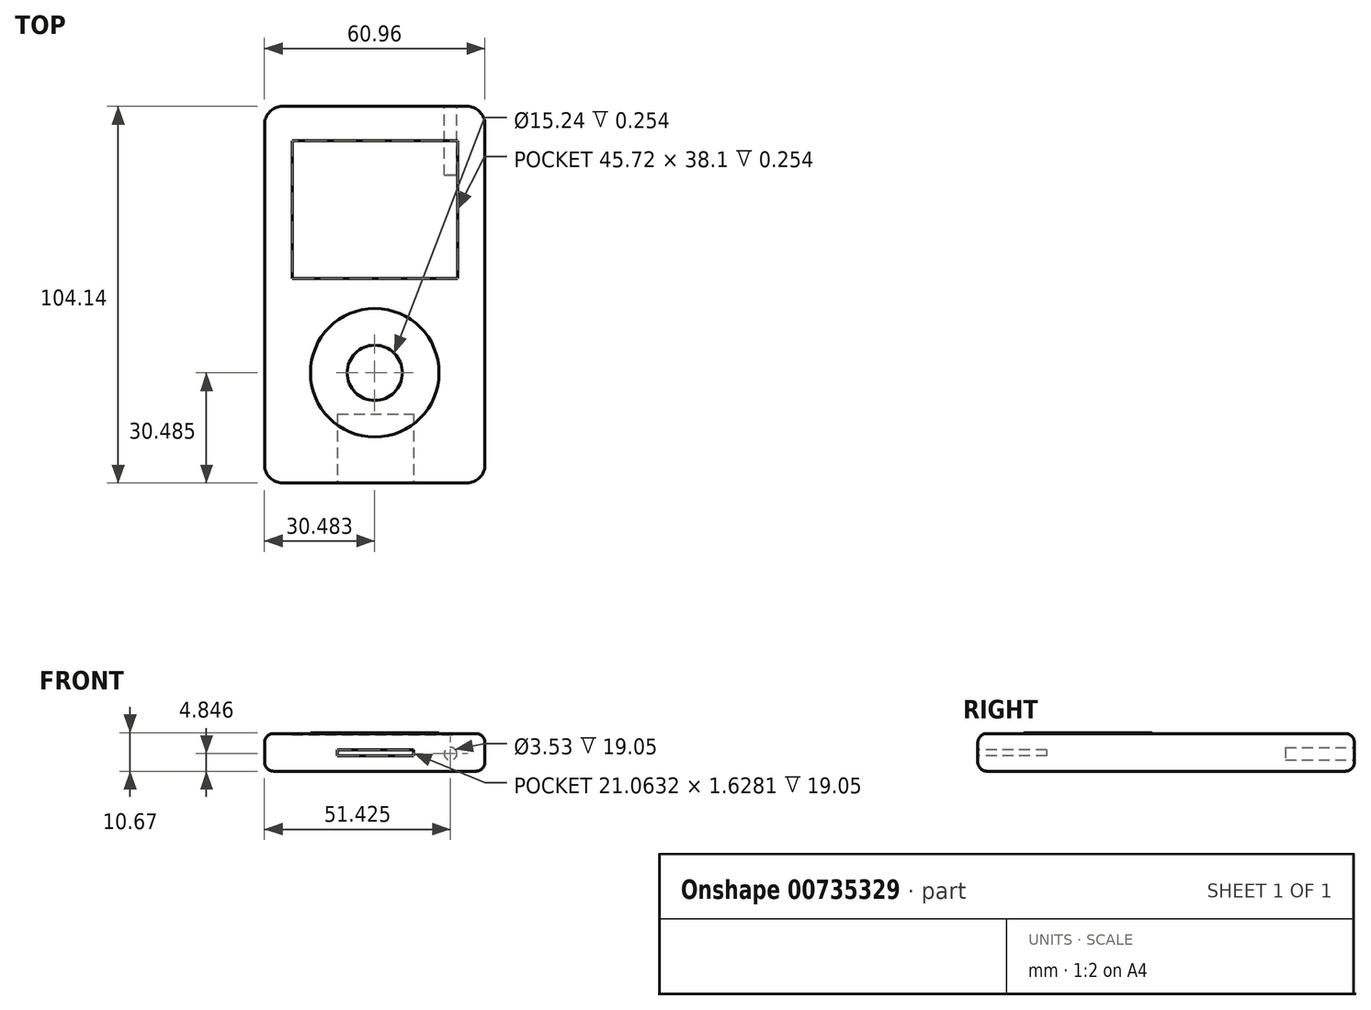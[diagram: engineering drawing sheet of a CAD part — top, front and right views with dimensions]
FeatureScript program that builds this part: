
annotation { "Feature Type Name" : "Feature", "Feature Type Description" : "" }
export const myFeature = defineFeature(function(context is Context, id is Id, definition is map)
    precondition{}
    {
        {
            var Q0;
            Q0=qCreatedBy(makeId("Top.planeOp"),FACE);
            var sketch = newSketch(context, id + "F0", { "sketchPlane" : qUnion([Q0])});
            skLineSegment(sketch, "E0.bottom", {"start": v(-38.1, 48.27) * mm, "end": v(22.85, 48.27) * mm});
            skLineSegment(sketch, "E0.top", {"start": v(-38.1, -55.87) * mm, "end": v(22.85, -55.87) * mm});
            skLineSegment(sketch, "E0.left", {"start": v(-38.1, 48.27) * mm, "end": v(-38.1, -55.87) * mm});
            skLineSegment(sketch, "E0.right", {"start": v(22.85, 48.27) * mm, "end": v(22.85, -55.87) * mm});
            skSolve(sketch);
        }
        {
            var Q0;
            Q0=makeQuery(id+"F0.imprint","IMPRINT",FACE,{"disambiguationData":[TD([[makeQuery(id+"F0.imprint","IMPRINT",EDGE,{"derivedFrom":sQuery(id+"F0.wireOp",EDGE,"E0.bottom")}),-1.0]])]});
            extrude(context, id + "F1", {"entities" : qUnion([Q0]), "depth" : 10.4 * mm, "offsetDistance" : 25.4 * mm});
        }
        {
            var Q0;
            Q0=makeQuery(id+"F1.opExtrude","SWEPT_EDGE",EDGE,{"disambiguationData":[OSD([sQuery(id+"F0.wireOp",EDGE,"E0.bottom"),sQuery(id+"F0.wireOp",EDGE,"E0.right")])]});
            var Q1;
            Q1=makeQuery(id+"F1.opExtrude","SWEPT_EDGE",EDGE,{"disambiguationData":[OSD([sQuery(id+"F0.wireOp",EDGE,"E0.bottom"),sQuery(id+"F0.wireOp",EDGE,"E0.left")])]});
            var Q2;
            Q2=makeQuery(id+"F1.opExtrude","SWEPT_EDGE",EDGE,{"disambiguationData":[OSD([sQuery(id+"F0.wireOp",EDGE,"E0.top"),sQuery(id+"F0.wireOp",EDGE,"E0.right")])]});
            var Q3;
            Q3=makeQuery(id+"F1.opExtrude","SWEPT_EDGE",EDGE,{"disambiguationData":[OSD([sQuery(id+"F0.wireOp",EDGE,"E0.top"),sQuery(id+"F0.wireOp",EDGE,"E0.left")])]});
            fillet(context, id + "F2", {"entities" : qUnion([Q0, Q1, Q2, Q3]), "radius" : 5.08 * mm, "tangentPropagation" : true, "allowEdgeOverflow" : false});
        }
        {
            var Q0;
            Q0=makeQuery(id+"F1.opExtrude","CAP_FACE",FACE,{"disambiguationData":[OSD([sQuery(id+"F0.wireOp",EDGE,"E0.bottom"),sQuery(id+"F0.wireOp",EDGE,"E0.top"),sQuery(id+"F0.wireOp",EDGE,"E0.left"),sQuery(id+"F0.wireOp",EDGE,"E0.right")])],"isStart":false});
            var sketch = newSketch(context, id + "F3", { "sketchPlane" : qUnion([Q0])});
            skCircle(sketch, "E1", {"center": v(-7.63, -25.39) * mm, "radius": 17.78 * mm});
            skCircle(sketch, "E2", {"center": v(-7.63, -25.39) * mm, "radius": 7.62 * mm});
            skSolve(sketch);
        }
        {
            var Q0;
            Q0=makeQuery(id+"F3.imprint","IMPRINT",FACE,{"disambiguationData":[TD([[makeQuery(id+"F3.imprint","IMPRINT",EDGE,{"derivedFrom":sQuery(id+"F3.wireOp",EDGE,"E1")}),1.0]])]});
            extrude(context, id + "F4", {"entities" : qUnion([Q0]), "operationType" : NewBodyOperationType.ADD, "depth" : 0.25 * mm, "offsetDistance" : 25.4 * mm});
        }
        {
            var Q0;
            Q0=makeQuery(id+"F1.opExtrude","CAP_EDGE",EDGE,{"disambiguationData":[OSD([sQuery(id+"F0.wireOp",EDGE,"E0.right")])],"isStart":false});
            var Q1;
            Q1=makeQuery(id+"F1.opExtrude","CAP_EDGE",EDGE,{"disambiguationData":[OSD([sQuery(id+"F0.wireOp",EDGE,"E0.left")])],"isStart":true});
            fillet(context, id + "F5", {"entities" : qUnion([Q0, Q1]), "radius" : 2.54 * mm, "tangentPropagation" : true, "allowEdgeOverflow" : false});
        }
        {
            var Q0;
            {var subQ0=sQuery(id+"F0.wireOp",EDGE,"E0.left");var subQ1=sQuery(id+"F0.wireOp",EDGE,"E0.bottom");var subQ2=sQuery(id+"F0.wireOp",EDGE,"E0.top");var subQ3=sQuery(id+"F0.wireOp",EDGE,"E0.right");Q0=makeQuery(id+"F4.boolean.opBoolean","SPLIT",FACE,{"disambiguationData":[TD([makeQuery(id+"F1.opExtrude","SWEPT_FACE",FACE,{"disambiguationData":[OSD([subQ1])]})])],"derivedFrom":makeQuery(id+"F1.opExtrude","CAP_FACE",FACE,{"disambiguationData":[OSD([subQ1,subQ2,subQ0,subQ3])],"isStart":false})});}
            var sketch = newSketch(context, id + "F6", { "sketchPlane" : qUnion([Q0])});
            skLineSegment(sketch, "E3.bottom", {"start": v(-30.49, 38.76) * mm, "end": v(15.23, 38.76) * mm});
            skLineSegment(sketch, "E3.top", {"start": v(-30.49, 0.66) * mm, "end": v(15.23, 0.66) * mm});
            skLineSegment(sketch, "E3.left", {"start": v(-30.49, 38.76) * mm, "end": v(-30.49, 0.66) * mm});
            skLineSegment(sketch, "E3.right", {"start": v(15.23, 38.76) * mm, "end": v(15.23, 0.66) * mm});
            skSolve(sketch);
        }
        {
            var Q0;
            Q0=makeQuery(id+"F6.imprint","IMPRINT",FACE,{"disambiguationData":[TD([[makeQuery(id+"F6.imprint","IMPRINT",EDGE,{"derivedFrom":sQuery(id+"F6.wireOp",EDGE,"E3.bottom")}),-1.0]])]});
            extrude(context, id + "F7", {"entities" : qUnion([Q0]), "operationType" : NewBodyOperationType.REMOVE, "oppositeDirection" : true, "depth" : 0.25 * mm, "offsetDistance" : 25.4 * mm});
        }
        {
            var Q0;
            Q0=makeQuery(id+"F1.opExtrude","SWEPT_FACE",FACE,{"disambiguationData":[OSD([sQuery(id+"F0.wireOp",EDGE,"E0.bottom")])]});
            var sketch = newSketch(context, id + "F8", { "sketchPlane" : qUnion([Q0])});
            skCircle(sketch, "E4", {"center": v(-13.31, 4.85) * mm, "radius": 1.76 * mm});
            skSolve(sketch);
        }
        {
            var Q0;
            Q0=makeQuery(id+"F8.imprint","IMPRINT",FACE,{"disambiguationData":[TD([[makeQuery(id+"F8.imprint","IMPRINT",EDGE,{"derivedFrom":sQuery(id+"F8.wireOp",EDGE,"E4")}),1.0]])]});
            extrude(context, id + "F9", {"entities" : qUnion([Q0]), "operationType" : NewBodyOperationType.REMOVE, "oppositeDirection" : true, "depth" : 19.05 * mm, "offsetDistance" : 25.4 * mm});
        }
        {
            var Q0;
            Q0=makeQuery(id+"F1.opExtrude","SWEPT_FACE",FACE,{"disambiguationData":[OSD([sQuery(id+"F0.wireOp",EDGE,"E0.top")])]});
            var sketch = newSketch(context, id + "F10", { "sketchPlane" : qUnion([Q0])});
            skLineSegment(sketch, "E5.bottom", {"start": v(-17.94, 5.87) * mm, "end": v(3.12, 5.87) * mm});
            skLineSegment(sketch, "E5.top", {"start": v(-17.94, 4.24) * mm, "end": v(3.12, 4.24) * mm});
            skLineSegment(sketch, "E5.left", {"start": v(-17.94, 5.87) * mm, "end": v(-17.94, 4.24) * mm});
            skLineSegment(sketch, "E5.right", {"start": v(3.12, 5.87) * mm, "end": v(3.12, 4.24) * mm});
            skSolve(sketch);
        }
        {
            var Q0;
            Q0=makeQuery(id+"F10.imprint","IMPRINT",FACE,{"disambiguationData":[TD([[makeQuery(id+"F10.imprint","IMPRINT",EDGE,{"derivedFrom":sQuery(id+"F10.wireOp",EDGE,"E5.bottom")}),-1.0]])]});
            extrude(context, id + "F11", {"entities" : qUnion([Q0]), "operationType" : NewBodyOperationType.REMOVE, "oppositeDirection" : true, "depth" : 19.05 * mm, "offsetDistance" : 25.4 * mm});
        }
    });
